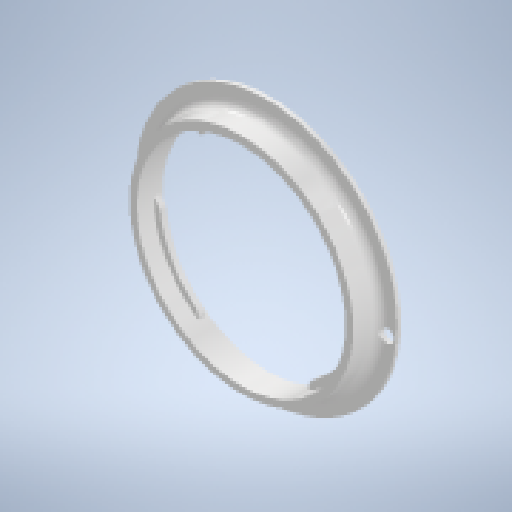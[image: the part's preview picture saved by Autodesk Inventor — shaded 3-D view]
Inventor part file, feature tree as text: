
AUTODESK INVENTOR PART (.ipt)
format: ipt  version: 2023 (Build 270158000, 158)  size: 877,568 bytes
history: native  units: mm
features: extrude x8, other x2, sketch x1, fillet x1
ambient origin geometry x8: Origin, YZ Plane, XZ Plane, XY Plane, X Axis, Y Axis, Z Axis, Center Point
bodies: Body1 (feature_tree)
feature tree (12):
  other  "CE2_adaptor_thin_2_v7"
  sketch  "Schizzo6"
  extrude  "Estrusione7"  Depth=1.0mm TaperAngle=0.0deg
  extrude  "Estrusione8"  Depth=7.0mm TaperAngle=0.0deg
  extrude  "Estrusione9"  Depth=3.0mm TaperAngle=0.0deg
  extrude  "Estrusione10"  Depth=4.75mm TaperAngle=0.0deg
  extrude  "Estrusione11"  Depth=3.0mm TaperAngle=0.0deg
  extrude  "Estrusione12"  Depth=1.6mm TaperAngle=0.0deg
  extrude  "Estrusione13"  Depth=1.6mm TaperAngle=0.0deg
  extrude  "Estrusione14"  Depth=0.9mm TaperAngle=0.0deg
  fillet  "Raccordo3"  Radius=53.0mm
  other  "Lavorazione mesh1"
